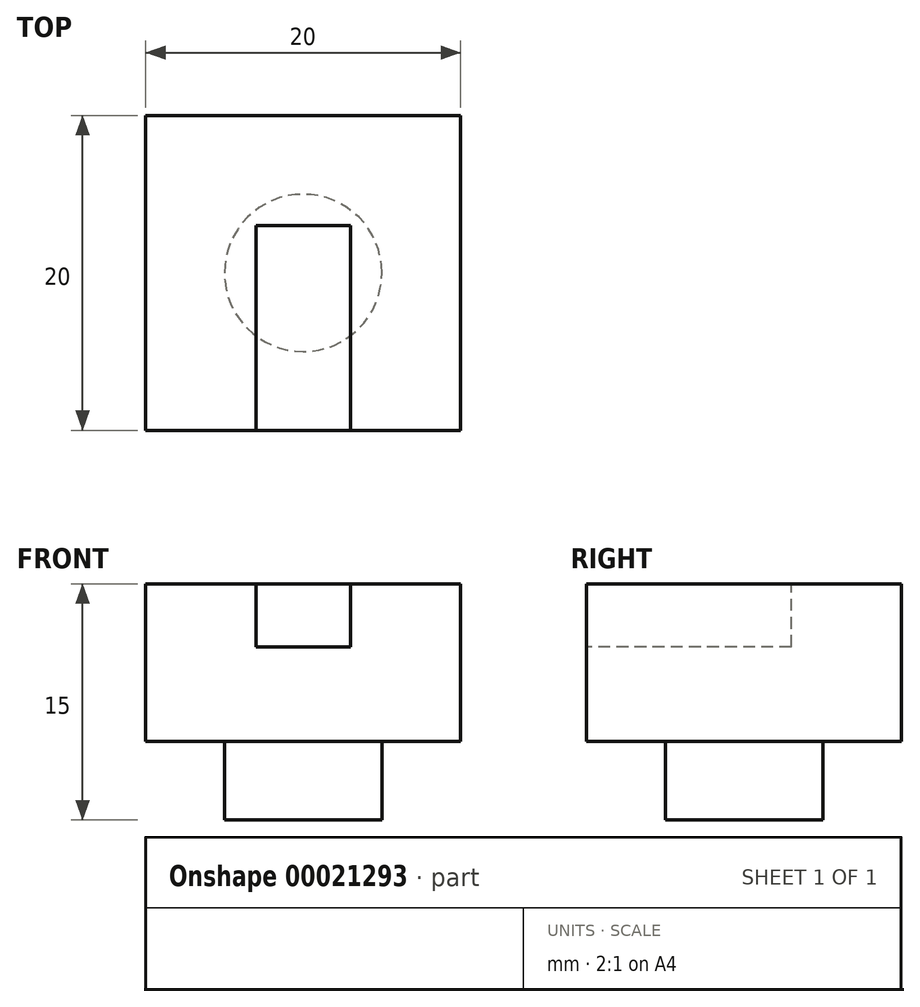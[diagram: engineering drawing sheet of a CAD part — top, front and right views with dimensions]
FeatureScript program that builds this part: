
annotation { "Feature Type Name" : "Feature", "Feature Type Description" : "" }
export const myFeature = defineFeature(function(context is Context, id is Id, definition is map)
    precondition{}
    {
        {
            var Q0;
            Q0=qCreatedBy(makeId("Top.planeOp"),FACE);
            var sketch = newSketch(context, id + "F0", { "sketchPlane" : qUnion([Q0])});
            skCircle(sketch, "E0", {"center": v(0, 0) * mm, "radius": 5 * mm});
            skSolve(sketch);
        }
        {
            var Q0;
            Q0 = qSketchRegion(id + "F0", true);
            extrude(context, id + "F1", {"entities" : qUnion([Q0]), "depth" : 5 * mm});
        }
        {
            var Q0;
            Q0=makeQuery(id+"F1.opExtrude","CAP_FACE",FACE,{"disambiguationData":[OSD([sQuery(id+"F0.wireOp",EDGE,"E0")])],"isStart":false});
            var sketch = newSketch(context, id + "F2", { "sketchPlane" : qUnion([Q0])});
            skLineSegment(sketch, "E1.rect.bottom", {"start": v(10, -10) * mm, "end": v(-10, -10) * mm});
            skLineSegment(sketch, "E1.rect.top", {"start": v(10, 10) * mm, "end": v(-10, 10) * mm});
            skLineSegment(sketch, "E1.rect.left", {"start": v(10, -10) * mm, "end": v(10, 10) * mm});
            skLineSegment(sketch, "E1.rect.right", {"start": v(-10, -10) * mm, "end": v(-10, 10) * mm});
            skPoint(sketch, "E1.rect.middle", {"position": v(0, 0) * mm});
            skSolve(sketch);
        }
        {
            var Q0;
            Q0 = qSketchRegion(id + "F2", true);
            extrude(context, id + "F3", {"entities" : qUnion([Q0]), "operationType" : NewBodyOperationType.ADD, "depth" : 10 * mm});
        }
        {
            var Q0;
            Q0=makeQuery(id+"F3.opExtrude","CAP_FACE",FACE,{"disambiguationData":[OSD([sQuery(id+"F2.wireOp",EDGE,"E1.rect.bottom"),sQuery(id+"F2.wireOp",EDGE,"E1.rect.top"),sQuery(id+"F2.wireOp",EDGE,"E1.rect.left"),sQuery(id+"F2.wireOp",EDGE,"E1.rect.right")])],"isStart":false});
            var sketch = newSketch(context, id + "F4", { "sketchPlane" : qUnion([Q0])});
            skLineSegment(sketch, "E2.bottom", {"start": v(-3, 3) * mm, "end": v(3, 3) * mm});
            skLineSegment(sketch, "E2.top", {"start": v(-3, -10) * mm, "end": v(3, -10) * mm});
            skLineSegment(sketch, "E2.left", {"start": v(-3, 3) * mm, "end": v(-3, -10) * mm});
            skLineSegment(sketch, "E2.right", {"start": v(3, 3) * mm, "end": v(3, -10) * mm});
            skSolve(sketch);
        }
        {
            var Q0;
            Q0 = qSketchRegion(id + "F4", true);
            extrude(context, id + "F5", {"entities" : qUnion([Q0]), "operationType" : NewBodyOperationType.REMOVE, "oppositeDirection" : true, "depth" : 4 * mm});
        }
    });
